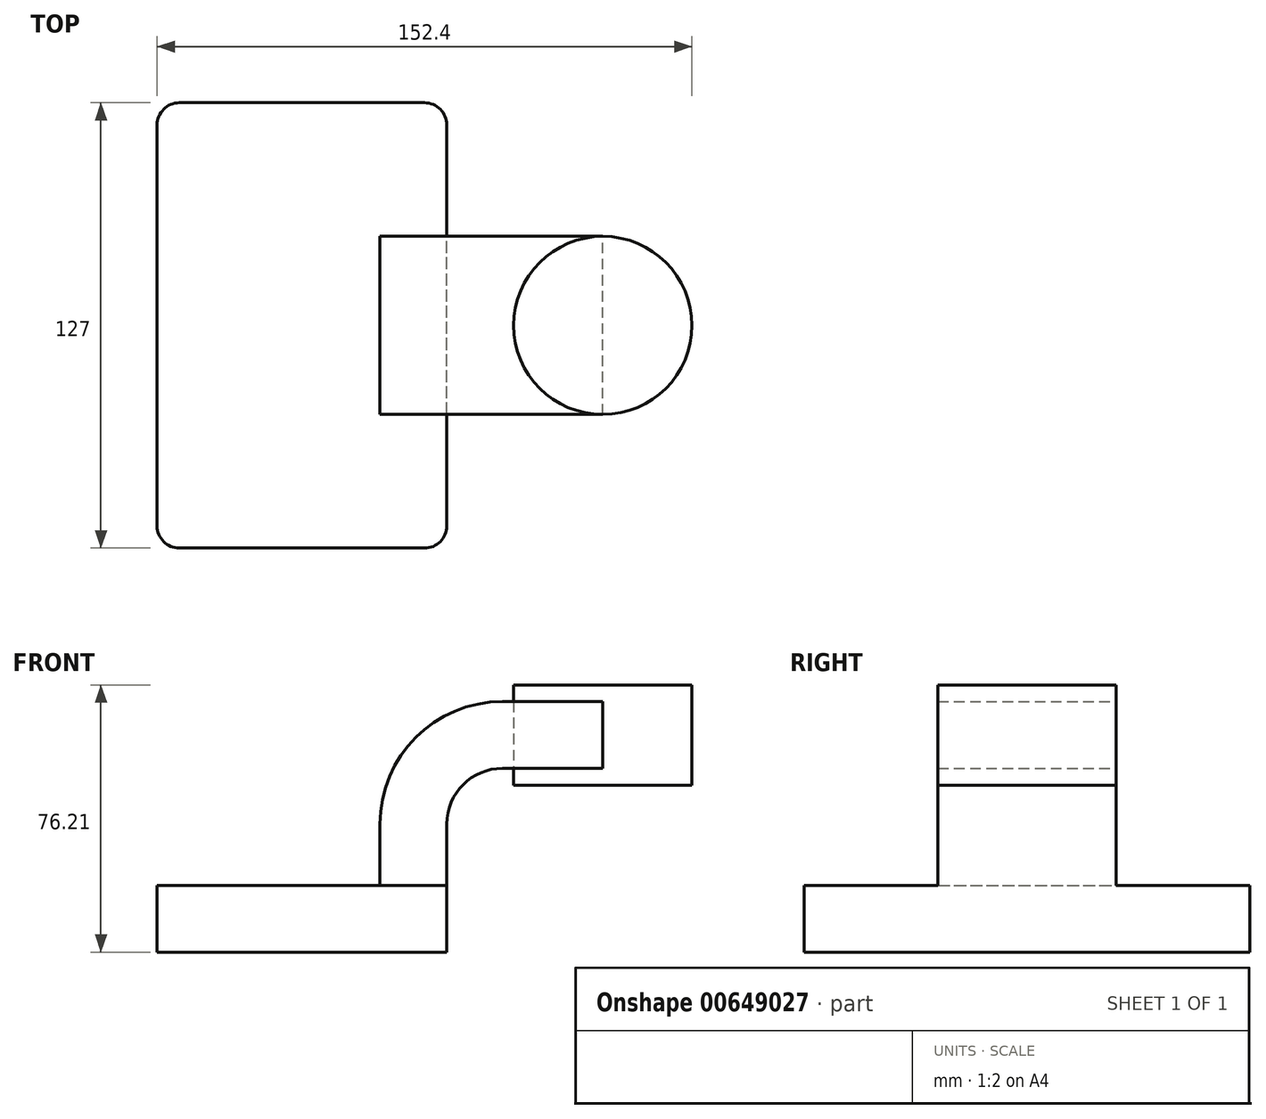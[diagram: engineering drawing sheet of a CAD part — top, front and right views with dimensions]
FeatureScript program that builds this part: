
annotation { "Feature Type Name" : "Feature", "Feature Type Description" : "" }
export const myFeature = defineFeature(function(context is Context, id is Id, definition is map)
    precondition{}
    {
        {
            var Q0;
            Q0=qCreatedBy(makeId("Front.planeOp"),FACE);
            var sketch = newSketch(context, id + "F0", { "sketchPlane" : qUnion([Q0])});
            skLineSegment(sketch, "E0.bottom", {"start": v(41.28, -9.52) * mm, "end": v(-41.28, -9.53) * mm});
            skLineSegment(sketch, "E0.top", {"start": v(41.28, 9.53) * mm, "end": v(-41.28, 9.52) * mm});
            skLineSegment(sketch, "E0.left", {"start": v(41.28, -9.53) * mm, "end": v(41.28, 9.53) * mm});
            skLineSegment(sketch, "E0.right", {"start": v(-41.27, -9.53) * mm, "end": v(-41.28, 9.52) * mm});
            skPoint(sketch, "E0.middle", {"position": v(0, 0) * mm});
            skLineSegment(sketch, "E1.bottom", {"start": v(111.13, 38.1) * mm, "end": v(60.33, 38.1) * mm});
            skLineSegment(sketch, "E1.top", {"start": v(111.13, 66.68) * mm, "end": v(60.33, 66.68) * mm});
            skLineSegment(sketch, "E1.left", {"start": v(111.13, 38.1) * mm, "end": v(111.13, 66.68) * mm});
            skLineSegment(sketch, "E1.right", {"start": v(60.33, 38.1) * mm, "end": v(60.33, 66.68) * mm});
            skPoint(sketch, "E1.middle", {"position": v(85.73, 52.39) * mm});
            skLineSegment(sketch, "E2", {"start": v(41.27, 9.53) * mm, "end": v(41.27, 27) * mm});
            skArc(sketch, "E3", {"start": v(41.27, 27) * mm, "mid": v(45.92, 38.23) * mm, "end": v(57.15, 42.88) * mm});
            skLineSegment(sketch, "E4", {"start": v(57.15, 42.88) * mm, "end": v(85.73, 42.88) * mm});
            skLineSegment(sketch, "E5.0", {"start": v(57.15, 61.93) * mm, "end": v(85.73, 61.93) * mm});
            skArc(sketch, "E5.1", {"start": v(22.23, 27) * mm, "mid": v(32.45, 51.7) * mm, "end": v(57.15, 61.93) * mm});
            skLineSegment(sketch, "E5.2", {"start": v(22.22, 9.52) * mm, "end": v(22.22, 27) * mm});
            skLineSegment(sketch, "E6", {"start": v(85.73, 38.1) * mm, "end": v(85.73, 66.68) * mm});
            skFitSpline(sketch, "E7", {"points": [v(-41.28, 9.52) * mm, v(57.15, 61.93) * mm], "startDerivative": vector(38.3, 77.78) * mm, "endDerivative": vector(135.55, -6.56) * mm});
            skSolve(sketch);
        }
        {
            var Q0;
            Q0=makeQuery(id+"F0.imprint","IMPRINT",FACE,{"disambiguationData":[TD([[makeQuery(id+"F0.imprint","IMPRINT",EDGE,{"derivedFrom":sQuery(id+"F0.wireOp",EDGE,"E0.bottom")}),-1.0]])]});
            extrude(context, id + "F1", {"entities" : qUnion([Q0]), "endBound" : BoundingType.SYMMETRIC, "depth" : 127 * mm, "offsetDistance" : 25.4 * mm});
        }
        {
            var Q0;
            {var subQ1=sQuery(id+"F0.wireOp",EDGE,"E2");Q0=makeQuery(id+"F0.imprint","IMPRINT",FACE,{"disambiguationData":[TD([[makeQuery(id+"F0.imprint","IMPRINT",EDGE,{"derivedFrom":subQ1}),1.0]])]});}
            var Q1;
            {var subQ0=sQuery(id+"F0.wireOp",EDGE,"E4");var subQ1=sQuery(id+"F0.wireOp",EDGE,"E1.right");var subQ2=makeQuery(id+"F0.imprint","INTERSECT",VERTEX,{"derivedFrom":[subQ1,subQ0]});Q1=makeQuery(id+"F0.imprint","IMPRINT",FACE,{"disambiguationData":[TD([[makeQuery(id+"F0.imprint","IMPRINT",EDGE,{"disambiguationData":[TD([[subQ2,-1.0]])],"derivedFrom":subQ1}),-1.0]])]});}
            extrude(context, id + "F2", {"entities" : qUnion([Q0, Q1]), "operationType" : NewBodyOperationType.ADD, "endBound" : BoundingType.SYMMETRIC, "depth" : 50.8 * mm, "offsetDistance" : 25.4 * mm});
        }
        {
            var Q0;
            Q0=makeQuery(id+"F0.imprint","IMPRINT",FACE,{"disambiguationData":[TD([[makeQuery(id+"F0.imprint","IMPRINT",EDGE,{"derivedFrom":sQuery(id+"F0.wireOp",EDGE,"E5.1")}),1.0]])]});
            extrude(context, id + "F3", {"entities" : qUnion([Q0]), "operationType" : NewBodyOperationType.ADD, "endBound" : BoundingType.SYMMETRIC, "depth" : 15.88 * mm, "offsetDistance" : 25.4 * mm});
        }
        {
            var Q0;
            {var subQ4=sQuery(id+"F0.wireOp",EDGE,"E1.left");Q0=makeQuery(id+"F0.imprint","IMPRINT",FACE,{"disambiguationData":[TD([[makeQuery(id+"F0.imprint","IMPRINT",EDGE,{"derivedFrom":subQ4}),1.0]])]});}
            var Q1;
            Q1=sQuery(id+"F0.wireOp",EDGE,"E6");
            revolve(context, id + "F4", {"entities" : qUnion([Q0]), "axis" : qUnion([Q1]), "revolveType" : RevolveType.FULL});
        }
        {
            var Q0;
            Q0=makeQuery(id+"F1.opExtrude","CAP_EDGE",EDGE,{"disambiguationData":[OSD([sQuery(id+"F0.wireOp",EDGE,"E0.left")])],"isStart":false});
            var Q1;
            Q1=makeQuery(id+"F1.opExtrude","CAP_EDGE",EDGE,{"disambiguationData":[OSD([sQuery(id+"F0.wireOp",EDGE,"E0.right")])],"isStart":false});
            var Q2;
            Q2=makeQuery(id+"F1.opExtrude","CAP_EDGE",EDGE,{"disambiguationData":[OSD([sQuery(id+"F0.wireOp",EDGE,"E0.left")])],"isStart":true});
            var Q3;
            Q3=makeQuery(id+"F1.opExtrude","CAP_EDGE",EDGE,{"disambiguationData":[OSD([sQuery(id+"F0.wireOp",EDGE,"E0.right")])],"isStart":true});
            fillet(context, id + "F5", {"entities" : qUnion([Q0, Q1, Q2, Q3]), "radius" : 6.35 * mm, "tangentPropagation" : true, "allowEdgeOverflow" : false});
        }
    });
